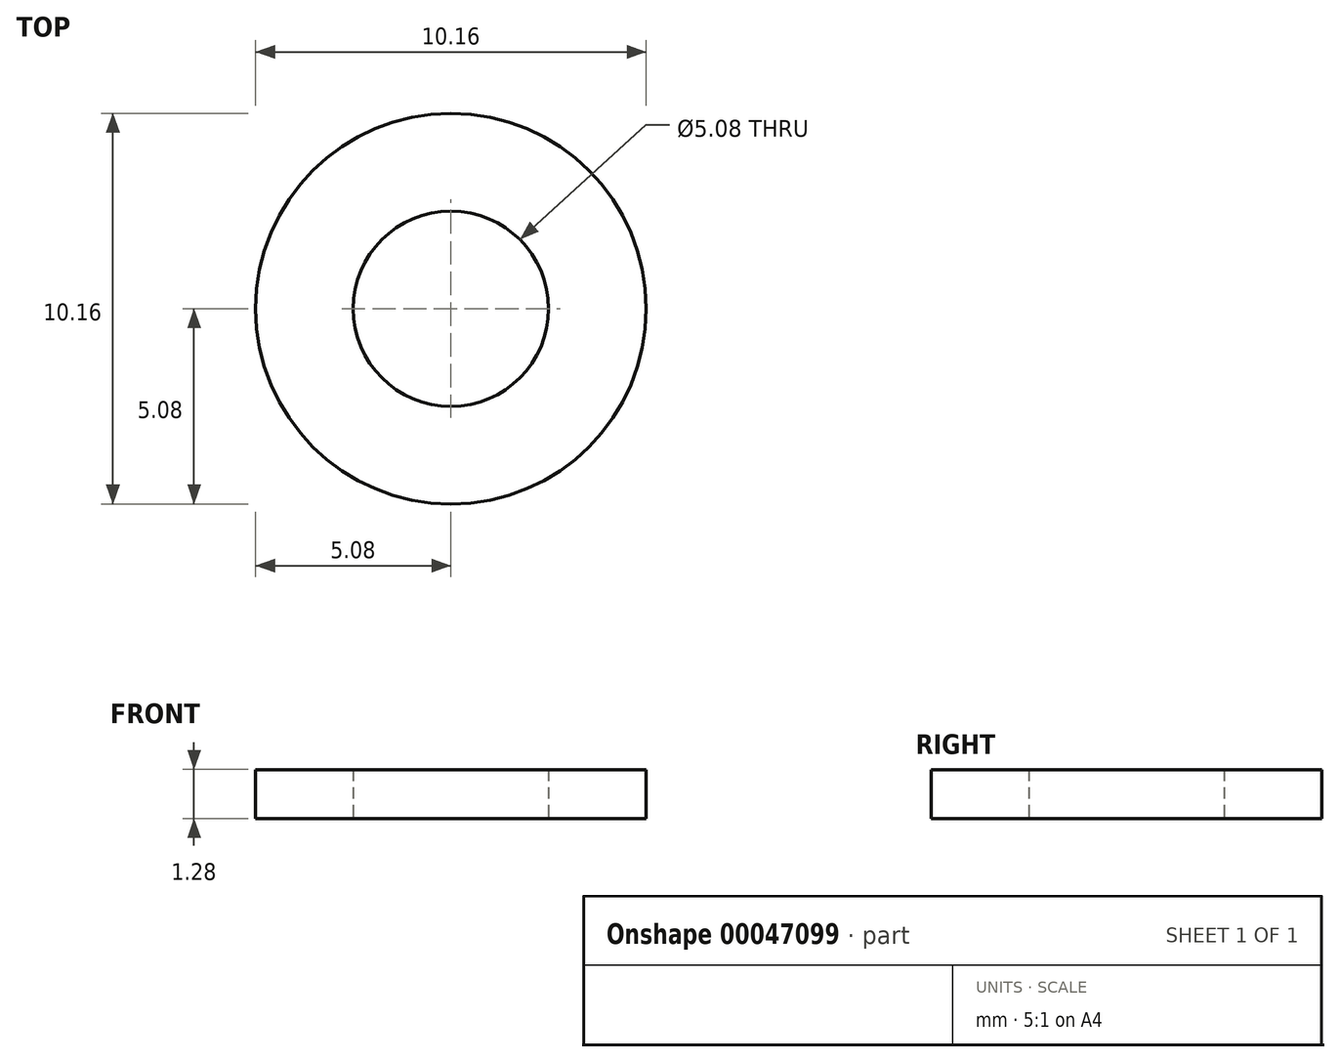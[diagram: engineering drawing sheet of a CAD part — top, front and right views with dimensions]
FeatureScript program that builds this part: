
annotation { "Feature Type Name" : "Feature", "Feature Type Description" : "" }
export const myFeature = defineFeature(function(context is Context, id is Id, definition is map)
    precondition{}
    {
        {
            var Q0;
            Q0=qCreatedBy(makeId("Top.planeOp"),FACE);
            var sketch = newSketch(context, id + "F0", { "sketchPlane" : qUnion([Q0])});
            skCircle(sketch, "E0", {"center": v(0, 0) * mm, "radius": 5.08 * mm});
            skCircle(sketch, "E1", {"center": v(0, 0) * mm, "radius": 2.54 * mm});
            skSolve(sketch);
        }
        {
            var Q0;
            Q0=makeQuery(id+"F0.imprint","IMPRINT",FACE,{"disambiguationData":[TD([[makeQuery(id+"F0.imprint","IMPRINT",EDGE,{"derivedFrom":sQuery(id+"F0.wireOp",EDGE,"E0")}),1.0]])]});
            var sketch = newSketch(context, id + "F1", { "sketchPlane" : qUnion([Q0])});
            skSolve(sketch);
        }
        {
            var Q0;
            Q0 = qSketchRegion(id + "F1", true);
            var Q1;
            Q1=makeQuery(id+"F0.imprint","IMPRINT",FACE,{"disambiguationData":[TD([[makeQuery(id+"F0.imprint","IMPRINT",EDGE,{"derivedFrom":sQuery(id+"F0.wireOp",EDGE,"E0")}),1.0]])]});
            extrude(context, id + "F2", {"entities" : qUnion([Q0, Q1]), "endBound" : BoundingType.SYMMETRIC, "depth" : 1.27 * mm});
        }
    });
